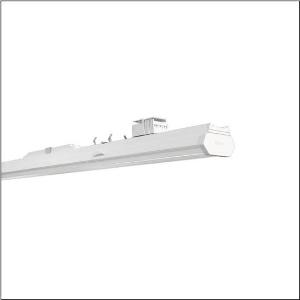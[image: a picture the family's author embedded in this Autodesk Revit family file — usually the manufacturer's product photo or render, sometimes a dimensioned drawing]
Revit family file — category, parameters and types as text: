
# Revit family: licross_r__21_protected_ho_52td12mn4e5m_88f3
name_source: partatom
category: Lighting Fixtures
units: mm (PartAtom-declared; Revit-internal decimal feet)

## family parameters
Cut with Voids When Loaded = No
Host = Face
Light Source = No
Part Type = Normal
Room Calculation Point = No
Round Connector Dimension = Use Diameter
Shared = No

## types (1)
- --- (1 x LED, 14780 lm, 83.2 W, 4000K)
    Apparent Load = 83 VA
    CIE Flux Codes = 70 91 97 98 100
    Color Rendering = 80
    Color Temperature = 4000K
    Default Elevation = 1800 mm
    Description = Licross® 21 Protected HO, luminaire insert, of sheet steel, galvanised, coil coated, white, length: 1.500mm, width: 90mm, height: 101mm, LED rated luminous flux: 14.790lm, light colour: 840, SDCM (Standard Deviation of Colour Matching)MacAdam ≤ 3 SDCM (initial), control gear: ON/OFF Multilumen, with plug, 3-pole, with phase selection, mains connection: 220..240V, AC, 50/60Hz, rated input power: 83W, internal wiring halogen-free, primary light control with lens, of plastic, primary optical cover: cover, of PMMA, light emission: direct distribution, primary light characteristic: symmetric, protection rating (complete): IP54, insulation class (complete): insulation class I (protective earthing), certification: CE, ENEC, VDE, UKCA, protection symbol: D if used in an environment with non-conductive dust loads with corresponding accessories, impact resistance: IK06, permissible ambient temperature for indoor applications: -35..+35°C, corresponds to IFS (International Featured Standards) requirements for safety and quality in the food industry, reducing of maximum allowable ambient temperature of 5°C with ceiling mounting, LABS conformity tested according to VDMA 24364:2018-05, packaging unit: 1 piece
    Height = 92 mm
    Lamp = 1 x LED
    Lamp Light Flux = 14780 lm
    Lamp Power = 83.2 W
    Lamp count = 1
    Length = 1500 mm
    Luminous efficacy = 178 lm/W
    Manufacturer = Siteco
    ModVariant = No
    Model = 52TD12MN4E5M
    Mounting Place = Ceiling
    Mounting Type = Pendant
    Number of Poles = 1
    OnlyDefault = Yes
    Power Factor = 1
    Product Name = Licross® 21 Protected HO
    Product group = luminaire insert | ceiling pendant
    ProductGroupID = 901
    Protection Class = Protection class I
    Protection Degree = IP 54
    RLX_Detail_Level = 1
    RLX_Emergency_Light_Flux = 0 lm
    RLX_Emergency_Type = 0
    RLX_Emergency_Type_DB = No
    RlxData = <blob elided: 22141 chars, md5=65fa40a2>
    Socket = socket
    Standby Power = 0 W
    System Light Flux = 14780 lm
    System Power = 83 W
    Type Comments = factory setting: luminous flux: 100 % | (A | C | E) | 195 mA
    Type Image = l_1256148.jpg
    URL = http://relux.com
    VarID = @adj_113077
    Voltage = 0 V
    Weight = 0.00 kg
    Width = 88 mm

## geometry (parser evidence)
native form markers: Blend x4, Sweep x9
no freeform markers — native parametric forms only
